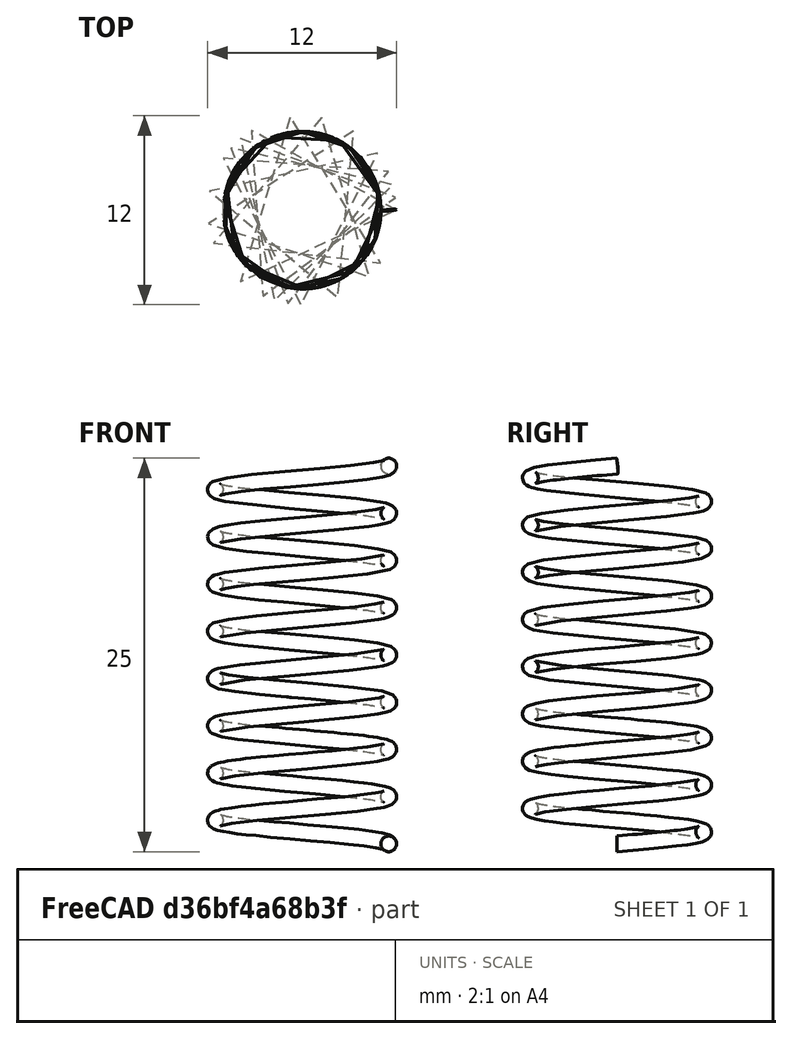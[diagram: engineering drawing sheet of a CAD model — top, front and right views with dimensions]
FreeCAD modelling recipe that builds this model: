
FCSTD DOCUMENT  (FreeCAD 1.0R39109 (Git))
Label: 15_3_lead_screw_flange
License: All rights reserved
LicenseURL: https://en.wikipedia.org/wiki/All_rights_reserved
objects: Part::Helix×1, PartDesign::SubShapeBinder×1, Sketcher::SketchObject×1, PartDesign::AdditivePipe×1, PartDesign::Body×1
note: 8 computed .brp shape members not serialized (recipe doc carries the construction recipe); baked Part::Feature solids carry a one-line shape summary decoded from their .brp

FEATURE [Part::Helix] Helix001
  Angle = 0
  AttacherType = Attacher::AttachEngine3D
  Height = 24
  Length = 277.5
  LocalCoord = 0
  Pitch = 3
  Radius = 5.5
  SegmentLength = 0
  Style = 1
FEATURE [PartDesign::SubShapeBinder] Binder
  BindCopyOnChange = 0
  BindMode = 0
  ClaimChildren = false
  Context = -> Body [Binder.]
  Fuse = false
  MakeFace = true
  OffsetFill = false
  OffsetIntersection = false
  OffsetJoinType = 0
  OffsetOpenResult = false
  PartialLoad = false
  Refine = true
  Relative = true
  Support = -> [Helix001]
  _Version = 2
FEATURE [Sketcher::SketchObject] Sketch
  ArcFitTolerance = 1e-06
  AttachmentSupport = -> [XZ_Plane]
  ExternalGeometry = -> [Binder]
  FullyConstrained = true
  MakeInternals = false
  MapMode = 5
  Placement = pos=(0,0,0) rot=(1,0,0;1.5708rad)
  sketch-geometry (1):
    g0: Circle CenterX=5.5 CenterY=0 CenterZ=0 NormalX=0 NormalY=0 NormalZ=1 AngleXU=0 Radius=0.5
  constraints (2):
    c: Coincident(g0,g-3)
    c: Diameter(g0) = 1
FEATURE [PartDesign::AdditivePipe] AdditivePipe
  AuxilleryCurvelinear = true
  AuxillerySpineTangent = false
  Binormal = (0,0,0)
  Mode = 0
  Placement = pos=(0,0,0) rot=(1,0,0;1.5708rad)
  Profile = -> Sketch
  Refine = true
  Spine = -> Binder
  SpineTangent = false
  Suppressed = false
  Transformation = 0
  Transition = 0
FEATURE [PartDesign::Body] Body
  AllowCompound = false
  Group = -> [Binder,Sketch,AdditivePipe]
  Origin = -> Origin
  Tip = -> AdditivePipe
